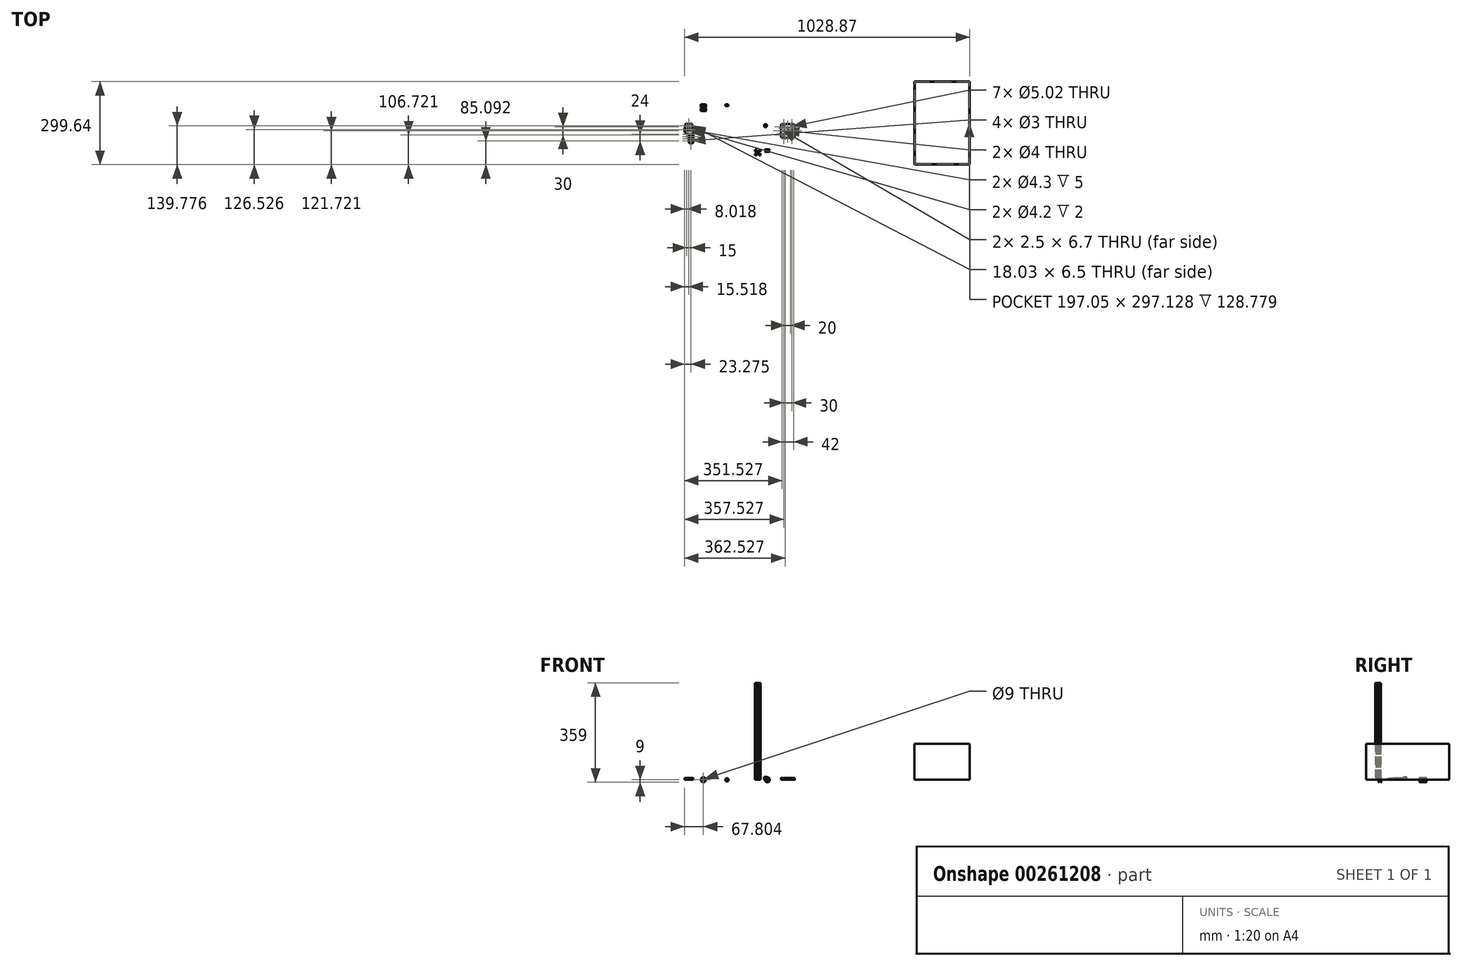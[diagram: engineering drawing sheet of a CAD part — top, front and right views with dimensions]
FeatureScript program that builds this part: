
annotation { "Feature Type Name" : "Feature", "Feature Type Description" : "" }
export const myFeature = defineFeature(function(context is Context, id is Id, definition is map)
    precondition{}
    {
        {
            var Q0;
            Q0=qCreatedBy(makeId("Top.planeOp"),FACE);
            var sketch = newSketch(context, id + "F0", { "sketchPlane" : qUnion([Q0])});
            skCircle(sketch, "E0", {"center": v(46.6, 59.24) * mm, "radius": 5.5 * mm});
            skCircle(sketch, "E1", {"center": v(46.6, 59.24) * mm, "radius": 2.5 * mm});
            skSolve(sketch);
        }
        {
            var Q0;
            Q0=qSketchRegion(id+"F0",true);
            extrude(context, id + "F1", {"entities" : qUnion([Q0]), "depth" : 11 * mm});
        }
        {
            var Q0;
            Q0=qCreatedBy(makeId("Top.planeOp"),FACE);
            var sketch = newSketch(context, id + "F2", { "sketchPlane" : qUnion([Q0])});
            skLineSegment(sketch, "E2.bottom", {"start": v(108.1, 65.37) * mm, "end": v(145.76, 65.37) * mm});
            skLineSegment(sketch, "E2.top", {"start": v(108.1, 15.37) * mm, "end": v(145.76, 15.37) * mm});
            skLineSegment(sketch, "E2.left", {"start": v(101.93, 59.2) * mm, "end": v(101.93, 21.54) * mm});
            skLineSegment(sketch, "E2.right", {"start": v(151.93, 59.2) * mm, "end": v(151.93, 21.54) * mm});
            skCircle(sketch, "E3", {"center": v(126.93, 40.37) * mm, "radius": 2.5 * mm});
            skPoint(sketch, "E3.centerSnap0", {"position": v(151.93, 40.37) * mm});
            skPoint(sketch, "E3.centerSnap1", {"position": v(126.93, 65.37) * mm});
            skLineSegment(sketch, "E4", {"start": v(126.93, 40.37) * mm, "end": v(126.93, 50.37) * mm, "construction": true});
            skLineSegment(sketch, "E5", {"start": v(126.93, 40.37) * mm, "end": v(136.93, 40.37) * mm, "construction": true});
            skCircle(sketch, "E6", {"center": v(126.93, 50.37) * mm, "radius": 2.5 * mm});
            skCircle(sketch, "E7", {"center": v(136.93, 40.37) * mm, "radius": 2 * mm});
            skLineSegment(sketch, "E8.MirrorCS", {"start": v(126.93, 40.37) * mm, "end": v(126.93, 30.37) * mm, "construction": true});
            skCircle(sketch, "E9.MirrorC", {"center": v(126.93, 30.37) * mm, "radius": 2.5 * mm});
            skLineSegment(sketch, "E10.MirrorCS", {"start": v(126.93, 40.37) * mm, "end": v(116.93, 40.37) * mm, "construction": true});
            skCircle(sketch, "E11.MirrorC", {"center": v(116.93, 40.37) * mm, "radius": 2 * mm});
            skPoint(sketch, "E12.visualSharp", {"position": v(101.93, 65.37) * mm});
            skArc(sketch, "E12.filletArc", {"start": v(108.1, 65.37) * mm, "mid": v(103.73, 63.56) * mm, "end": v(101.93, 59.2) * mm});
            skPoint(sketch, "E13.visualSharp", {"position": v(151.93, 65.37) * mm});
            skArc(sketch, "E13.filletArc", {"start": v(151.93, 59.2) * mm, "mid": v(150.12, 63.56) * mm, "end": v(145.76, 65.37) * mm});
            skPoint(sketch, "E14.visualSharp", {"position": v(151.93, 15.37) * mm});
            skArc(sketch, "E14.filletArc", {"start": v(145.76, 15.37) * mm, "mid": v(150.12, 17.18) * mm, "end": v(151.93, 21.54) * mm});
            skPoint(sketch, "E15.visualSharp", {"position": v(101.93, 15.37) * mm});
            skArc(sketch, "E15.filletArc", {"start": v(101.93, 21.54) * mm, "mid": v(103.73, 17.18) * mm, "end": v(108.1, 15.37) * mm});
            skLineSegment(sketch, "E16.left", {"start": v(101.93, 40.37) * mm, "end": v(101.93, 42.37) * mm, "construction": true});
            skLineSegment(sketch, "E17", {"start": v(101.93, 15.37) * mm, "end": v(151.93, 65.37) * mm, "construction": true});
            skLineSegment(sketch, "E18", {"start": v(126.93, 65.37) * mm, "end": v(141.93, 65.37) * mm, "construction": true});
            skLineSegment(sketch, "E19.MirrorCS", {"start": v(126.93, 65.37) * mm, "end": v(111.93, 65.37) * mm, "construction": true});
            skLineSegment(sketch, "E20.MirrorCS", {"start": v(126.93, 15.37) * mm, "end": v(111.93, 15.37) * mm, "construction": true});
            skLineSegment(sketch, "E21.MirrorCS", {"start": v(126.93, 15.37) * mm, "end": v(141.93, 15.37) * mm, "construction": true});
            skLineSegment(sketch, "E22.MirrorCS", {"start": v(101.93, 40.37) * mm, "end": v(101.93, 25.37) * mm, "construction": true});
            skLineSegment(sketch, "E23.MirrorCS", {"start": v(101.93, 40.37) * mm, "end": v(101.93, 55.37) * mm, "construction": true});
            skLineSegment(sketch, "E24.MirrorCS", {"start": v(151.93, 40.37) * mm, "end": v(151.93, 55.37) * mm, "construction": true});
            skLineSegment(sketch, "E25.MirrorCS", {"start": v(151.93, 40.37) * mm, "end": v(151.93, 25.37) * mm, "construction": true});
            skCircle(sketch, "E26", {"center": v(111.93, 55.37) * mm, "radius": 2.5 * mm});
            skCircle(sketch, "E27.MirrorC", {"center": v(141.93, 25.37) * mm, "radius": 2.5 * mm});
            skCircle(sketch, "E28.MirrorC", {"center": v(111.93, 25.37) * mm, "radius": 2.5 * mm});
            skCircle(sketch, "E29.MirrorC", {"center": v(141.93, 55.37) * mm, "radius": 2.5 * mm});
            skLineSegment(sketch, "E30.top", {"start": v(101.93, 43.72) * mm, "end": v(107.18, 43.72) * mm});
            skLineSegment(sketch, "E30.left", {"start": v(101.93, 40.37) * mm, "end": v(101.93, 43.72) * mm});
            skLineSegment(sketch, "E30.right", {"start": v(107.18, 40.37) * mm, "end": v(107.18, 43.72) * mm});
            skLineSegment(sketch, "E31.MirrorCS", {"start": v(107.18, 40.37) * mm, "end": v(107.18, 37.02) * mm});
            skLineSegment(sketch, "E32.MirrorCS", {"start": v(101.93, 37.02) * mm, "end": v(107.18, 37.02) * mm});
            skLineSegment(sketch, "E33", {"start": v(104.68, 43.72) * mm, "end": v(104.68, 37.02) * mm});
            skPoint(sketch, "E33.startSnap0", {"position": v(104.55, 43.72) * mm});
            skPoint(sketch, "E34.end.orphan", {"position": v(104.68, 41.53) * mm});
            skLineSegment(sketch, "E35.MirrorCS", {"start": v(146.68, 40.37) * mm, "end": v(146.68, 37.02) * mm});
            skLineSegment(sketch, "E36.MirrorCS", {"start": v(146.68, 40.37) * mm, "end": v(146.68, 43.72) * mm});
            skLineSegment(sketch, "E37.MirrorCS", {"start": v(151.93, 43.72) * mm, "end": v(146.68, 43.72) * mm});
            skLineSegment(sketch, "E38.MirrorCS", {"start": v(149.18, 43.72) * mm, "end": v(149.18, 37.02) * mm});
            skLineSegment(sketch, "E39.MirrorCS", {"start": v(151.93, 37.02) * mm, "end": v(146.68, 37.02) * mm});
            skSolve(sketch);
        }
        {
            var Q0;
            Q0=qSketchRegion(id+"F2",true);
            extrude(context, id + "F3", {"entities" : qUnion([Q0]), "depth" : 6.35 * mm});
        }
        {
            var Q0;
            Q0=qCreatedBy(makeId("Top.planeOp"),FACE);
            var sketch = newSketch(context, id + "F4", { "sketchPlane" : qUnion([Q0])});
            skLineSegment(sketch, "E40", {"start": v(-177.8, 135.87) * mm, "end": v(-177.8, 111.87) * mm});
            skLineSegment(sketch, "E41", {"start": v(-173.3, 111.87) * mm, "end": v(-168.8, 111.87) * mm});
            skLineSegment(sketch, "E42", {"start": v(-173.3, 135.87) * mm, "end": v(-173.3, 111.87) * mm});
            skLineSegment(sketch, "E43", {"start": v(-168.8, 111.87) * mm, "end": v(-168.8, 120.15) * mm});
            skLineSegment(sketch, "E44", {"start": v(-168.8, 135.87) * mm, "end": v(-173.3, 135.87) * mm});
            skLineSegment(sketch, "E45", {"start": v(-173.3, 117.29) * mm, "end": v(-168.8, 118.75) * mm});
            skLineSegment(sketch, "E46", {"start": v(-168.8, 118.75) * mm, "end": v(-168.8, 120.15) * mm});
            skLineSegment(sketch, "E47", {"start": v(-168.8, 120.15) * mm, "end": v(-173.3, 118.68) * mm});
            skLineSegment(sketch, "E48", {"start": v(-173.3, 118.68) * mm, "end": v(-173.3, 120.43) * mm});
            skLineSegment(sketch, "E49", {"start": v(-173.3, 120.43) * mm, "end": v(-168.8, 121.9) * mm});
            skLineSegment(sketch, "E50", {"start": v(-168.8, 121.9) * mm, "end": v(-168.8, 123.87) * mm});
            skLineSegment(sketch, "E51", {"start": v(-168.8, 123.87) * mm, "end": v(-173.3, 122.4) * mm});
            skLineSegment(sketch, "E52", {"start": v(-173.3, 122.4) * mm, "end": v(-173.3, 124.62) * mm});
            skLineSegment(sketch, "E53", {"start": v(-173.3, 124.62) * mm, "end": v(-168.8, 126.08) * mm});
            skLineSegment(sketch, "E54", {"start": v(-168.8, 126.08) * mm, "end": v(-168.8, 128.1) * mm});
            skLineSegment(sketch, "E55", {"start": v(-168.8, 128.1) * mm, "end": v(-173.3, 126.64) * mm});
            skLineSegment(sketch, "E56", {"start": v(-173.3, 126.64) * mm, "end": v(-173.3, 128.46) * mm});
            skLineSegment(sketch, "E57", {"start": v(-173.3, 128.46) * mm, "end": v(-168.8, 129.92) * mm});
            skLineSegment(sketch, "E58.trimOffspring", {"start": v(-168.8, 129.92) * mm, "end": v(-168.8, 135.87) * mm});
            skLineSegment(sketch, "E59", {"start": v(-172.4, 128.75) * mm, "end": v(-172.4, 117.58) * mm});
            skSolve(sketch);
        }
        {
            var Q0;
            Q0=qSketchRegion(id+"F4",true);
            var Q1;
            Q1=sQuery(id+"F4.wireOp",EDGE,"E40");
            revolve(context, id + "F5", {"entities" : qUnion([Q0]), "axis" : qUnion([Q1]), "revolveType" : RevolveType.FULL});
        }
        {
            var Q0;
            Q0=qCreatedBy(makeId("Top.planeOp"),FACE);
            var sketch = newSketch(context, id + "F6", { "sketchPlane" : qUnion([Q0])});
            skLineSegment(sketch, "E60", {"start": v(-87.76, 135.55) * mm, "end": v(-87.76, 130.55) * mm});
            skLineSegment(sketch, "E61", {"start": v(-87.76, 130.55) * mm, "end": v(-86.76, 130.55) * mm});
            skLineSegment(sketch, "E62", {"start": v(-86.76, 130.55) * mm, "end": v(-86.76, 129.55) * mm});
            skLineSegment(sketch, "E63", {"start": v(-86.76, 129.55) * mm, "end": v(-87.76, 129.55) * mm});
            skLineSegment(sketch, "E64", {"start": v(-87.76, 135.55) * mm, "end": v(-89.76, 135.55) * mm});
            skLineSegment(sketch, "E65", {"start": v(-92.76, 129.55) * mm, "end": v(-92.76, 135.55) * mm, "construction": true});
            skLineSegment(sketch, "E66", {"start": v(-89.76, 135.55) * mm, "end": v(-89.76, 129.55) * mm});
            skLineSegment(sketch, "E67", {"start": v(-92.76, 129.55) * mm, "end": v(-89.76, 129.55) * mm});
            skLineSegment(sketch, "E68", {"start": v(-87.76, 129.55) * mm, "end": v(-89.76, 129.55) * mm});
            skSolve(sketch);
        }
        {
            var Q0;
            Q0=makeQuery(id+"F6.imprint","IMPRINT",FACE,{"disambiguationData":[TD([[makeQuery(id+"F6.imprint","IMPRINT",EDGE,{"derivedFrom":sQuery(id+"F6.wireOp",EDGE,"E60")}),-1.0]])]});
            var Q1;
            Q1=sQuery(id+"F6.wireOp",EDGE,"E65");
            revolve(context, id + "F7", {"entities" : qUnion([Q0]), "axis" : qUnion([Q1]), "revolveType" : RevolveType.FULL});
        }
        {
            var Q0;
            Q0=qCreatedBy(makeId("Top.planeOp"),FACE);
            var sketch = newSketch(context, id + "F8", { "sketchPlane" : qUnion([Q0])});
            skLineSegment(sketch, "E69.bottom", {"start": v(-245.6, 55.18) * mm, "end": v(-214.57, 55.18) * mm});
            skCircle(sketch, "E70", {"center": v(-237.58, 45.18) * mm, "radius": 2.15 * mm});
            skCircle(sketch, "E71", {"center": v(-222.58, 45.18) * mm, "radius": 2.15 * mm});
            skLineSegment(sketch, "E72", {"start": v(-245.6, 55.18) * mm, "end": v(-245.6, 35.18) * mm});
            skLineSegment(sketch, "E73", {"start": v(-230.08, -4.26) * mm, "end": v(-214.57, -4.26) * mm});
            skLineSegment(sketch, "E74", {"start": v(-230.08, 27.74) * mm, "end": v(-230.08, -4.26) * mm});
            skLineSegment(sketch, "E75", {"start": v(-245.6, 35.18) * mm, "end": v(-230.08, 27.74) * mm});
            skLineSegment(sketch, "E76", {"start": v(-214.57, 55.18) * mm, "end": v(-214.57, -4.26) * mm});
            skCircle(sketch, "E77", {"center": v(-222.33, 3.74) * mm, "radius": 1.5 * mm});
            skCircle(sketch, "E78", {"center": v(-222.33, 11.74) * mm, "radius": 1.5 * mm});
            skCircle(sketch, "E79.MirrorC", {"center": v(-222.33, 19.74) * mm, "radius": 1.5 * mm});
            skCircle(sketch, "E80", {"center": v(-222.33, 27.74) * mm, "radius": 1.5 * mm});
            skLineSegment(sketch, "E81", {"start": v(-237.58, 45.18) * mm, "end": v(-222.58, 45.18) * mm, "construction": true});
            skLineSegment(sketch, "E82", {"start": v(-230.08, 55.18) * mm, "end": v(-230.08, 45.18) * mm, "construction": true});
            skLineSegment(sketch, "E83", {"start": v(-230.08, 45.18) * mm, "end": v(-230.08, 27.74) * mm, "construction": true});
            skSolve(sketch);
        }
        {
            var Q0;
            Q0=qSketchRegion(id+"F8",true);
            extrude(context, id + "F9", {"entities" : qUnion([Q0]), "depth" : 5 * mm});
        }
        {
            var Q0;
            Q0=makeQuery(id+"F9.opExtrude","SWEPT_EDGE",EDGE,{"disambiguationData":[OSD([sQuery(id+"F8.wireOp",EDGE,"E73"),sQuery(id+"F8.wireOp",EDGE,"E74")])]});
            var Q1;
            Q1=makeQuery(id+"F9.opExtrude","SWEPT_EDGE",EDGE,{"disambiguationData":[OSD([sQuery(id+"F8.wireOp",EDGE,"E73"),sQuery(id+"F8.wireOp",EDGE,"E76")])]});
            var Q2;
            Q2=makeQuery(id+"F9.opExtrude","SWEPT_EDGE",EDGE,{"disambiguationData":[OSD([sQuery(id+"F8.wireOp",EDGE,"E72"),sQuery(id+"F8.wireOp",EDGE,"E75")])]});
            var Q3;
            Q3=makeQuery(id+"F9.opExtrude","SWEPT_EDGE",EDGE,{"disambiguationData":[OSD([sQuery(id+"F8.wireOp",EDGE,"E69.bottom"),sQuery(id+"F8.wireOp",EDGE,"E76")])]});
            var Q4;
            Q4=makeQuery(id+"F9.opExtrude","SWEPT_EDGE",EDGE,{"disambiguationData":[OSD([sQuery(id+"F8.wireOp",EDGE,"E69.bottom"),sQuery(id+"F8.wireOp",EDGE,"E72")])]});
            chamfer(context, id + "F10", {"entities" : qUnion([Q0, Q1, Q2, Q3, Q4]), "width" : 3 * mm, "tangentPropagation" : true});
        }
        {
            var Q0;
            Q0=makeQuery(id+"F9.opExtrude","CAP_FACE",FACE,{"disambiguationData":[OSD([sQuery(id+"F8.wireOp",EDGE,"E69.bottom"),sQuery(id+"F8.wireOp",EDGE,"E70"),sQuery(id+"F8.wireOp",EDGE,"E71"),sQuery(id+"F8.wireOp",EDGE,"E72"),sQuery(id+"F8.wireOp",EDGE,"E73"),sQuery(id+"F8.wireOp",EDGE,"E74"),sQuery(id+"F8.wireOp",EDGE,"E75"),sQuery(id+"F8.wireOp",EDGE,"E76"),sQuery(id+"F8.wireOp",EDGE,"E77"),sQuery(id+"F8.wireOp",EDGE,"E78"),sQuery(id+"F8.wireOp",EDGE,"E79.MirrorC"),sQuery(id+"F8.wireOp",EDGE,"E80")])],"isStart":false});
            var sketch = newSketch(context, id + "F11", { "sketchPlane" : qUnion([Q0])});
            skLineSegment(sketch, "E84.top", {"start": v(-245.6, 47.67) * mm, "end": v(-214.57, 47.67) * mm});
            skLineSegment(sketch, "E84.right", {"start": v(-214.57, 44.62) * mm, "end": v(-214.57, 47.67) * mm});
            skLineSegment(sketch, "E85.MirrorCS", {"start": v(-245.6, 42.54) * mm, "end": v(-214.57, 42.54) * mm});
            skPoint(sketch, "E84.left.start.orphan", {"position": v(-245.6, 44.62) * mm});
            skLineSegment(sketch, "E86", {"start": v(-245.6, 47.67) * mm, "end": v(-245.6, 42.54) * mm});
            skLineSegment(sketch, "E87", {"start": v(-214.57, 44.62) * mm, "end": v(-214.57, 42.54) * mm});
            skCircle(sketch, "E88", {"center": v(-237.58, 45.18) * mm, "radius": 2.1 * mm});
            skCircle(sketch, "E89", {"center": v(-222.58, 45.18) * mm, "radius": 2.1 * mm});
            skSolve(sketch);
        }
        {
            var Q0;
            Q0=qSketchRegion(id+"F11",true);
            extrude(context, id + "F12", {"entities" : qUnion([Q0]), "operationType" : NewBodyOperationType.ADD, "depth" : 2 * mm});
        }
        {
            var Q0;
            {var subQ0=sQuery(id+"F8.wireOp",EDGE,"E75");var subQ1=sQuery(id+"F8.wireOp",EDGE,"E72");var subQ2=sQuery(id+"F8.wireOp",EDGE,"E80");var subQ3=sQuery(id+"F8.wireOp",EDGE,"E78");var subQ4=sQuery(id+"F8.wireOp",EDGE,"E79.MirrorC");var subQ5=sQuery(id+"F8.wireOp",EDGE,"E77");var subQ6=sQuery(id+"F8.wireOp",EDGE,"E76");var subQ7=sQuery(id+"F8.wireOp",EDGE,"E73");var subQ8=sQuery(id+"F8.wireOp",EDGE,"E74");Q0=makeQuery(id+"F12.boolean.opBoolean","SPLIT",FACE,{"disambiguationData":[TD([makeQuery(id+"F9.opExtrude","SWEPT_FACE",FACE,{"disambiguationData":[OSD([subQ7])]})])],"derivedFrom":makeQuery(id+"F9.opExtrude","CAP_FACE",FACE,{"disambiguationData":[OSD([sQuery(id+"F8.wireOp",EDGE,"E69.bottom"),sQuery(id+"F8.wireOp",EDGE,"E70"),sQuery(id+"F8.wireOp",EDGE,"E71"),subQ1,subQ7,subQ8,subQ0,subQ6,subQ5,subQ3,subQ4,subQ2])],"isStart":false})});}
            var sketch = newSketch(context, id + "F13", { "sketchPlane" : qUnion([Q0])});
            skCircle(sketch, "E90.cCircle", {"center": v(-222.33, 27.74) * mm, "radius": 2.85 * mm, "construction": true});
            skLineSegment(sketch, "E90.0", {"start": v(-219.03, 27.8) * mm, "end": v(-220.64, 24.92) * mm});
            skLineSegment(sketch, "E90.1", {"start": v(-220.64, 24.92) * mm, "end": v(-223.93, 24.87) * mm});
            skLineSegment(sketch, "E90.2", {"start": v(-223.93, 24.87) * mm, "end": v(-225.62, 27.69) * mm});
            skLineSegment(sketch, "E90.3", {"start": v(-225.62, 27.69) * mm, "end": v(-224.02, 30.57) * mm});
            skLineSegment(sketch, "E90.4", {"start": v(-224.02, 30.57) * mm, "end": v(-220.72, 30.62) * mm});
            skLineSegment(sketch, "E90.5", {"start": v(-220.72, 30.62) * mm, "end": v(-219.03, 27.8) * mm});
            skPoint(sketch, "E90.0.midPoint", {"position": v(-219.83, 26.36) * mm});
            skCircle(sketch, "E91.cCircle", {"center": v(-222.33, 19.74) * mm, "radius": 2.85 * mm, "construction": true});
            skLineSegment(sketch, "E91.0", {"start": v(-219.03, 19.78) * mm, "end": v(-220.65, 16.9) * mm});
            skLineSegment(sketch, "E91.1", {"start": v(-220.65, 16.9) * mm, "end": v(-223.94, 16.87) * mm});
            skLineSegment(sketch, "E91.2", {"start": v(-223.94, 16.87) * mm, "end": v(-225.62, 19.7) * mm});
            skLineSegment(sketch, "E91.3", {"start": v(-225.62, 19.7) * mm, "end": v(-224, 22.57) * mm});
            skLineSegment(sketch, "E91.4", {"start": v(-224, 22.57) * mm, "end": v(-220.7, 22.6) * mm});
            skLineSegment(sketch, "E91.5", {"start": v(-220.7, 22.6) * mm, "end": v(-219.03, 19.78) * mm});
            skPoint(sketch, "E91.0.midPoint", {"position": v(-219.84, 18.34) * mm});
            skCircle(sketch, "E92.cCircle", {"center": v(-222.33, 11.74) * mm, "radius": 2.85 * mm, "construction": true});
            skLineSegment(sketch, "E92.0", {"start": v(-220.72, 8.87) * mm, "end": v(-224.01, 8.92) * mm});
            skLineSegment(sketch, "E92.1", {"start": v(-224.01, 8.92) * mm, "end": v(-225.62, 11.79) * mm});
            skLineSegment(sketch, "E92.2", {"start": v(-225.62, 11.79) * mm, "end": v(-223.93, 14.61) * mm});
            skLineSegment(sketch, "E92.3", {"start": v(-223.93, 14.61) * mm, "end": v(-220.64, 14.57) * mm});
            skLineSegment(sketch, "E92.4", {"start": v(-220.64, 14.57) * mm, "end": v(-219.03, 11.7) * mm});
            skLineSegment(sketch, "E92.5", {"start": v(-219.03, 11.7) * mm, "end": v(-220.72, 8.87) * mm});
            skPoint(sketch, "E92.0.midPoint", {"position": v(-222.37, 8.9) * mm});
            skCircle(sketch, "E93.cCircle", {"center": v(-222.33, 3.74) * mm, "radius": 2.85 * mm, "construction": true});
            skLineSegment(sketch, "E93.0", {"start": v(-219.03, 3.72) * mm, "end": v(-220.7, 0.88) * mm});
            skLineSegment(sketch, "E93.1", {"start": v(-220.7, 0.88) * mm, "end": v(-224, 0.9) * mm});
            skLineSegment(sketch, "E93.2", {"start": v(-224, 0.9) * mm, "end": v(-225.62, 3.77) * mm});
            skLineSegment(sketch, "E93.3", {"start": v(-225.62, 3.77) * mm, "end": v(-223.95, 6.6) * mm});
            skLineSegment(sketch, "E93.4", {"start": v(-223.95, 6.6) * mm, "end": v(-220.66, 6.58) * mm});
            skLineSegment(sketch, "E93.5", {"start": v(-220.66, 6.58) * mm, "end": v(-219.03, 3.72) * mm});
            skPoint(sketch, "E93.0.midPoint", {"position": v(-219.87, 2.3) * mm});
            skSolve(sketch);
        }
        {
            var Q0;
            Q0=qSketchRegion(id+"F13",true);
            extrude(context, id + "F14", {"entities" : qUnion([Q0]), "operationType" : NewBodyOperationType.REMOVE, "oppositeDirection" : true, "depth" : 2 * mm});
        }
        {
            var Q0;
            Q0=makeQuery(id+"F9.opExtrude","CAP_FACE",FACE,{"disambiguationData":[OSD([sQuery(id+"F8.wireOp",EDGE,"E69.bottom"),sQuery(id+"F8.wireOp",EDGE,"E70"),sQuery(id+"F8.wireOp",EDGE,"E71"),sQuery(id+"F8.wireOp",EDGE,"E72"),sQuery(id+"F8.wireOp",EDGE,"E73"),sQuery(id+"F8.wireOp",EDGE,"E74"),sQuery(id+"F8.wireOp",EDGE,"E75"),sQuery(id+"F8.wireOp",EDGE,"E76"),sQuery(id+"F8.wireOp",EDGE,"E77"),sQuery(id+"F8.wireOp",EDGE,"E78"),sQuery(id+"F8.wireOp",EDGE,"E79.MirrorC"),sQuery(id+"F8.wireOp",EDGE,"E80")])],"isStart":true});
            var sketch = newSketch(context, id + "F15", { "sketchPlane" : qUnion([Q0])});
            skLineSegment(sketch, "E94.bottom", {"start": v(-242.6, -55.18) * mm, "end": v(-217.57, -55.18) * mm});
            skLineSegment(sketch, "E94.top", {"start": v(-242.6, -65.18) * mm, "end": v(-217.57, -65.18) * mm});
            skLineSegment(sketch, "E94.left", {"start": v(-242.6, -55.18) * mm, "end": v(-242.6, -65.18) * mm});
            skLineSegment(sketch, "E94.right", {"start": v(-217.57, -55.18) * mm, "end": v(-217.57, -65.18) * mm});
            skLineSegment(sketch, "E95.top", {"start": v(-239.1, -61.68) * mm, "end": v(-221.07, -61.68) * mm});
            skLineSegment(sketch, "E95.left", {"start": v(-242.6, -65.18) * mm, "end": v(-242.6, -61.68) * mm});
            skLineSegment(sketch, "E95.right", {"start": v(-217.57, -65.18) * mm, "end": v(-217.57, -61.68) * mm});
            skLineSegment(sketch, "E96.bottom", {"start": v(-242.6, -55.18) * mm, "end": v(-239.1, -55.18) * mm});
            skLineSegment(sketch, "E96.left", {"start": v(-242.6, -55.18) * mm, "end": v(-242.6, -61.68) * mm});
            skLineSegment(sketch, "E96.right", {"start": v(-239.1, -55.18) * mm, "end": v(-239.1, -61.68) * mm});
            skLineSegment(sketch, "E97.bottom", {"start": v(-217.57, -55.18) * mm, "end": v(-221.07, -55.18) * mm});
            skLineSegment(sketch, "E97.left", {"start": v(-217.57, -55.18) * mm, "end": v(-217.57, -61.68) * mm});
            skLineSegment(sketch, "E97.right", {"start": v(-221.07, -55.18) * mm, "end": v(-221.07, -61.68) * mm});
            skSolve(sketch);
        }
        {
            var Q0;
            Q0=makeQuery(id+"F15.imprint","IMPRINT",FACE,{"disambiguationData":[TD([[makeQuery(id+"F15.imprint","IMPRINT",EDGE,{"derivedFrom":sQuery(id+"F15.wireOp",EDGE,"E94.top")}),1.0]])]});
            extrude(context, id + "F16", {"entities" : qUnion([Q0]), "operationType" : NewBodyOperationType.ADD, "oppositeDirection" : true, "depth" : 5 * mm});
        }
        {
            var Q0;
            Q0=makeQuery(id+"F16.opExtrude","SWEPT_EDGE",EDGE,{"disambiguationData":[OSD([sQuery(id+"F15.wireOp",EDGE,"E94.top"),sQuery(id+"F15.wireOp",EDGE,"E95.left")])]});
            var Q1;
            Q1=makeQuery(id+"F16.opExtrude","SWEPT_EDGE",EDGE,{"disambiguationData":[OSD([sQuery(id+"F15.wireOp",EDGE,"E94.top"),sQuery(id+"F15.wireOp",EDGE,"E95.right")])]});
            chamfer(context, id + "F17", {"entities" : qUnion([Q0, Q1]), "width" : 2 * mm, "tangentPropagation" : true});
        }
        {
            var Q0;
            Q0=qCreatedBy(makeId("Top.planeOp"),FACE);
            var sketch = newSketch(context, id + "F18", { "sketchPlane" : qUnion([Q0])});
            skLineSegment(sketch, "E98.bottom", {"start": v(583.64, 218.3) * mm, "end": v(783.27, 218.3) * mm});
            skLineSegment(sketch, "E98.top", {"start": v(583.64, -81.35) * mm, "end": v(783.27, -81.35) * mm});
            skLineSegment(sketch, "E98.left", {"start": v(583.64, 218.3) * mm, "end": v(583.64, -81.35) * mm});
            skLineSegment(sketch, "E98.right", {"start": v(783.27, 218.3) * mm, "end": v(783.27, -81.35) * mm});
            skLineSegment(sketch, "E99.bottom", {"start": v(584.81, 216.9) * mm, "end": v(781.86, 216.9) * mm});
            skLineSegment(sketch, "E99.top", {"start": v(584.81, -80.23) * mm, "end": v(781.86, -80.23) * mm});
            skLineSegment(sketch, "E99.left", {"start": v(584.81, 216.9) * mm, "end": v(584.81, -80.23) * mm});
            skLineSegment(sketch, "E99.right", {"start": v(781.86, 216.9) * mm, "end": v(781.86, -80.23) * mm});
            skSolve(sketch);
        }
        {
            var Q0;
            Q0=qSketchRegion(id+"F18",true);
            extrude(context, id + "F19", {"entities" : qUnion([Q0]), "depth" : 129.78 * mm});
        }
        {
            var Q0;
            Q0=makeQuery(id+"FnAdPWIDGxTqRV2_20.opExtrude","CAP_FACE",FACE,{"disambiguationData":[OSD([sQuery(id+"FVg0QcCQKYEtaMn_20.wireOp",EDGE,"tovVjA8a-zPqJ-1KmD-G6D0-l0F1tnaQEWKl.bottom"),sQuery(id+"FVg0QcCQKYEtaMn_20.wireOp",EDGE,"tovVjA8a-zPqJ-1KmD-G6D0-l0F1tnaQEWKl.top"),sQuery(id+"FVg0QcCQKYEtaMn_20.wireOp",EDGE,"tovVjA8a-zPqJ-1KmD-G6D0-l0F1tnaQEWKl.left"),sQuery(id+"FVg0QcCQKYEtaMn_20.wireOp",EDGE,"tovVjA8a-zPqJ-1KmD-G6D0-l0F1tnaQEWKl.right"),sQuery(id+"FVg0QcCQKYEtaMn_20.wireOp",EDGE,"kqi9Kg9U-8iVR-4CjA-b6lG-PWRAAjiCiFc5"),sQuery(id+"FVg0QcCQKYEtaMn_20.wireOp",EDGE,"CbeHrla6-mjxN-cLcC-LonM-EPPCgRtVpuq4")])],"isStart":false});
            var sketch = newSketch(context, id + "F20", { "sketchPlane" : qUnion([Q0])});
            skLineSegment(sketch, "E100.bottom", {"start": v(102.54, -53.45) * mm, "end": v(147.54, -53.45) * mm});
            skLineSegment(sketch, "E100.top", {"start": v(102.54, -45.45) * mm, "end": v(147.54, -45.45) * mm});
            skLineSegment(sketch, "E100.left", {"start": v(102.54, -53.45) * mm, "end": v(102.54, -45.45) * mm});
            skLineSegment(sketch, "E100.right", {"start": v(147.54, -53.45) * mm, "end": v(147.54, -45.45) * mm});
            skSolve(sketch);
        }
        {
            var Q0;
            Q0=qCreatedBy(makeId("Top.planeOp"),FACE);
            var sketch = newSketch(context, id + "F21", { "sketchPlane" : qUnion([Q0])});
            skLineSegment(sketch, "E101.bottom", {"start": v(8.89, -27.7) * mm, "end": v(13.7, -27.7) * mm});
            skLineSegment(sketch, "E101.top", {"start": v(8.89, -47.7) * mm, "end": v(13.7, -47.7) * mm});
            skLineSegment(sketch, "E101.left", {"start": v(8.89, -27.7) * mm, "end": v(8.89, -32.51) * mm});
            skLineSegment(sketch, "E102.left", {"start": v(18.89, -27.7) * mm, "end": v(18.89, -29.5) * mm});
            skLineSegment(sketch, "E103", {"start": v(18.89, -27.7) * mm, "end": v(18.89, -47.7) * mm, "construction": true});
            skLineSegment(sketch, "E104", {"start": v(8.89, -37.7) * mm, "end": v(28.89, -37.7) * mm, "construction": true});
            skLineSegment(sketch, "E105.MirrorCS", {"start": v(15.5, -27.7) * mm, "end": v(15.5, -29.5) * mm, "construction": true});
            skLineSegment(sketch, "E106.MirrorCS", {"start": v(18.89, -29.5) * mm, "end": v(15.5, -29.5) * mm, "construction": true});
            skLineSegment(sketch, "E107", {"start": v(8.89, -27.7) * mm, "end": v(28.89, -47.7) * mm, "construction": true});
            skCircle(sketch, "E108", {"center": v(18.89, -37.7) * mm, "radius": 2.1 * mm});
            skLineSegment(sketch, "E109", {"start": v(15.5, -29.5) * mm, "end": v(13.7, -27.7) * mm});
            skLineSegment(sketch, "E110", {"start": v(18.89, -29.5) * mm, "end": v(18.89, -31.54) * mm});
            skLineSegment(sketch, "E111.left", {"start": v(15.5, -29.5) * mm, "end": v(15.5, -31.17) * mm, "construction": true});
            skLineSegment(sketch, "E112", {"start": v(13.74, -32.55) * mm, "end": v(14.24, -32.05) * mm});
            skLineSegment(sketch, "E113", {"start": v(14.24, -32.05) * mm, "end": v(13.36, -31.17) * mm});
            skLineSegment(sketch, "E114", {"start": v(13.36, -31.17) * mm, "end": v(13.36, -29.5) * mm});
            skLineSegment(sketch, "E115", {"start": v(13.36, -29.5) * mm, "end": v(15.5, -29.5) * mm});
            skLineSegment(sketch, "E116.bottom", {"start": v(15.5, -31.17) * mm, "end": v(18.89, -31.17) * mm, "construction": true});
            skLineSegment(sketch, "E117", {"start": v(14.24, -32.05) * mm, "end": v(16.05, -33.86) * mm});
            skPoint(sketch, "E116.left.end.orphan", {"position": v(16.05, -34.27) * mm});
            skLineSegment(sketch, "E118", {"start": v(16.05, -33.86) * mm, "end": v(18.89, -33.86) * mm});
            skLineSegment(sketch, "E119", {"start": v(17.6, -29.5) * mm, "end": v(17.6, -33.86) * mm, "construction": true});
            skLineSegment(sketch, "E120.MirrorCS", {"start": v(22.28, -29.5) * mm, "end": v(24.08, -27.7) * mm});
            skLineSegment(sketch, "E121.MirrorCS", {"start": v(24.42, -29.5) * mm, "end": v(22.28, -29.5) * mm});
            skLineSegment(sketch, "E122.MirrorCS", {"start": v(24.42, -31.17) * mm, "end": v(24.42, -29.5) * mm});
            skLineSegment(sketch, "E123.MirrorCS", {"start": v(23.53, -32.05) * mm, "end": v(24.42, -31.17) * mm});
            skLineSegment(sketch, "E124.MirrorCS", {"start": v(23.53, -32.05) * mm, "end": v(21.73, -33.86) * mm});
            skLineSegment(sketch, "E125.MirrorCS", {"start": v(21.73, -33.86) * mm, "end": v(18.89, -33.86) * mm});
            skLineSegment(sketch, "E126.MirrorCS", {"start": v(15.5, -45.9) * mm, "end": v(13.7, -47.7) * mm});
            skLineSegment(sketch, "E127.MirrorCS", {"start": v(13.36, -45.9) * mm, "end": v(15.5, -45.9) * mm});
            skLineSegment(sketch, "E128.MirrorCS", {"start": v(13.36, -44.23) * mm, "end": v(13.36, -45.9) * mm});
            skLineSegment(sketch, "E129.MirrorCS", {"start": v(14.24, -43.34) * mm, "end": v(13.36, -44.23) * mm});
            skLineSegment(sketch, "E130.MirrorCS", {"start": v(16.05, -41.54) * mm, "end": v(18.89, -41.54) * mm});
            skLineSegment(sketch, "E131.MirrorCS", {"start": v(21.73, -41.54) * mm, "end": v(18.89, -41.54) * mm});
            skLineSegment(sketch, "E132.MirrorCS", {"start": v(23.53, -43.34) * mm, "end": v(21.73, -41.54) * mm});
            skLineSegment(sketch, "E133.MirrorCS", {"start": v(23.53, -43.34) * mm, "end": v(24.42, -44.23) * mm});
            skLineSegment(sketch, "E134.MirrorCS", {"start": v(24.42, -44.23) * mm, "end": v(24.42, -45.9) * mm});
            skLineSegment(sketch, "E135.MirrorCS", {"start": v(24.42, -45.9) * mm, "end": v(22.28, -45.9) * mm});
            skLineSegment(sketch, "E136.MirrorCS", {"start": v(22.28, -45.9) * mm, "end": v(24.08, -47.7) * mm});
            skLineSegment(sketch, "E137.MirrorCS", {"start": v(14.24, -43.34) * mm, "end": v(16.05, -41.54) * mm});
            skLineSegment(sketch, "E138.MirrorCS", {"start": v(27.09, -32.17) * mm, "end": v(27.09, -34.31) * mm});
            skLineSegment(sketch, "E139.MirrorCS", {"start": v(27.09, -34.31) * mm, "end": v(28.89, -32.51) * mm});
            skLineSegment(sketch, "E140.MirrorCS", {"start": v(25.42, -32.17) * mm, "end": v(27.09, -32.17) * mm});
            skLineSegment(sketch, "E141.MirrorCS", {"start": v(24.54, -33.05) * mm, "end": v(25.42, -32.17) * mm});
            skLineSegment(sketch, "E142.MirrorCS", {"start": v(22.73, -34.86) * mm, "end": v(22.73, -37.7) * mm});
            skLineSegment(sketch, "E143.MirrorCS", {"start": v(22.73, -40.54) * mm, "end": v(22.73, -37.7) * mm});
            skLineSegment(sketch, "E144.MirrorCS", {"start": v(24.54, -42.34) * mm, "end": v(22.73, -40.54) * mm});
            skLineSegment(sketch, "E145.MirrorCS", {"start": v(24.54, -42.34) * mm, "end": v(25.42, -43.23) * mm});
            skLineSegment(sketch, "E146.MirrorCS", {"start": v(25.42, -43.23) * mm, "end": v(27.09, -43.23) * mm});
            skLineSegment(sketch, "E147.MirrorCS", {"start": v(27.09, -43.23) * mm, "end": v(27.09, -41.09) * mm});
            skLineSegment(sketch, "E148.MirrorCS", {"start": v(27.09, -41.09) * mm, "end": v(28.89, -42.89) * mm});
            skLineSegment(sketch, "E149.MirrorCS", {"start": v(24.54, -33.05) * mm, "end": v(22.73, -34.86) * mm});
            skLineSegment(sketch, "E150.MirrorCS", {"start": v(10.69, -34.31) * mm, "end": v(8.89, -32.51) * mm});
            skLineSegment(sketch, "E151.MirrorCS", {"start": v(10.69, -32.17) * mm, "end": v(10.69, -34.31) * mm});
            skLineSegment(sketch, "E152.MirrorCS", {"start": v(12.36, -32.17) * mm, "end": v(10.69, -32.17) * mm});
            skLineSegment(sketch, "E153.MirrorCS", {"start": v(13.24, -33.05) * mm, "end": v(12.36, -32.17) * mm});
            skLineSegment(sketch, "E154.MirrorCS", {"start": v(13.24, -33.05) * mm, "end": v(15.05, -34.86) * mm});
            skLineSegment(sketch, "E155.MirrorCS", {"start": v(15.05, -34.86) * mm, "end": v(15.05, -37.7) * mm});
            skLineSegment(sketch, "E156.MirrorCS", {"start": v(15.05, -40.54) * mm, "end": v(15.05, -37.7) * mm});
            skLineSegment(sketch, "E157.MirrorCS", {"start": v(13.24, -42.34) * mm, "end": v(15.05, -40.54) * mm});
            skLineSegment(sketch, "E158.MirrorCS", {"start": v(13.24, -42.34) * mm, "end": v(12.36, -43.23) * mm});
            skLineSegment(sketch, "E159.MirrorCS", {"start": v(12.36, -43.23) * mm, "end": v(10.69, -43.23) * mm});
            skLineSegment(sketch, "E160.MirrorCS", {"start": v(10.69, -43.23) * mm, "end": v(10.69, -41.09) * mm});
            skLineSegment(sketch, "E161.MirrorCS", {"start": v(10.69, -41.09) * mm, "end": v(8.89, -42.89) * mm});
            skLineSegment(sketch, "E162.trimOffspring", {"start": v(28.89, -42.89) * mm, "end": v(28.89, -47.7) * mm});
            skLineSegment(sketch, "E163.trimOffspring", {"start": v(24.08, -27.7) * mm, "end": v(28.89, -27.7) * mm});
            skLineSegment(sketch, "E164.trimOffspring", {"start": v(8.89, -42.89) * mm, "end": v(8.89, -47.7) * mm});
            skLineSegment(sketch, "E165.trimOffspring", {"start": v(24.08, -47.7) * mm, "end": v(28.89, -47.7) * mm});
            skLineSegment(sketch, "E166", {"start": v(28.89, -27.7) * mm, "end": v(28.89, -32.51) * mm});
            skLineSegment(sketch, "E167.bottom", {"start": v(18.89, -37.7) * mm, "end": v(25.39, -37.7) * mm});
            skLineSegment(sketch, "E167.top", {"start": v(18.89, -43.75) * mm, "end": v(25.39, -43.75) * mm, "construction": true});
            skLineSegment(sketch, "E167.left", {"start": v(18.89, -37.7) * mm, "end": v(18.89, -43.75) * mm});
            skLineSegment(sketch, "E167.right", {"start": v(25.39, -37.7) * mm, "end": v(25.39, -43.75) * mm, "construction": true});
            skSolve(sketch);
        }
        {
            var Q0;
            Q0=qSketchRegion(id+"F21",true);
            extrude(context, id + "F22", {"entities" : qUnion([Q0]), "depth" : 350 * mm});
        }
        {
            var Q0;
            Q0=qCreatedBy(makeId("Top.planeOp"),FACE);
            var sketch = newSketch(context, id + "F23", { "sketchPlane" : qUnion([Q0])});
            skLineSegment(sketch, "E168", {"start": v(54.5, -26.81) * mm, "end": v(54.5, -35.41) * mm});
            skLineSegment(sketch, "E169", {"start": v(54.5, -35.41) * mm, "end": v(59.5, -35.41) * mm});
            skLineSegment(sketch, "E170", {"start": v(54.5, -35.41) * mm, "end": v(62, -35.41) * mm});
            skLineSegment(sketch, "E171", {"start": v(59.5, -34.91) * mm, "end": v(59.5, -27.31) * mm});
            skLineSegment(sketch, "E172", {"start": v(54.5, -26.81) * mm, "end": v(62, -26.81) * mm});
            skLineSegment(sketch, "E173", {"start": v(62, -26.81) * mm, "end": v(62, -27.31) * mm});
            skLineSegment(sketch, "E174", {"start": v(62, -27.31) * mm, "end": v(59.5, -27.31) * mm});
            skLineSegment(sketch, "E175", {"start": v(62, -35.41) * mm, "end": v(62, -34.91) * mm});
            skLineSegment(sketch, "E176", {"start": v(62, -34.91) * mm, "end": v(59.5, -34.91) * mm});
            skLineSegment(sketch, "E177", {"start": v(54.5, -31.11) * mm, "end": v(53, -31.11) * mm, "construction": true});
            skLineSegment(sketch, "E178", {"start": v(53, -26.81) * mm, "end": v(53, -35.41) * mm});
            skPoint(sketch, "E179.orphan", {"position": v(59.5, -26.81) * mm});
            skSolve(sketch);
        }
        {
            var Q0;
            Q0=qSketchRegion(id+"F23",true);
            var Q1;
            Q1=sQuery(id+"F23.wireOp",EDGE,"E178");
            revolve(context, id + "F24", {"entities" : qUnion([Q0]), "axis" : qUnion([Q1]), "revolveType" : RevolveType.FULL});
        }
        {
            var Q0;
            Q0=makeQuery(id+"F18.imprint","IMPRINT",FACE,{"disambiguationData":[TD([[makeQuery(id+"F18.imprint","IMPRINT",EDGE,{"derivedFrom":sQuery(id+"F18.wireOp",EDGE,"E99.bottom")}),-1.0]])]});
            extrude(context, id + "F25", {"entities" : qUnion([Q0]), "operationType" : NewBodyOperationType.ADD, "depth" : 1 * mm});
        }
    });
